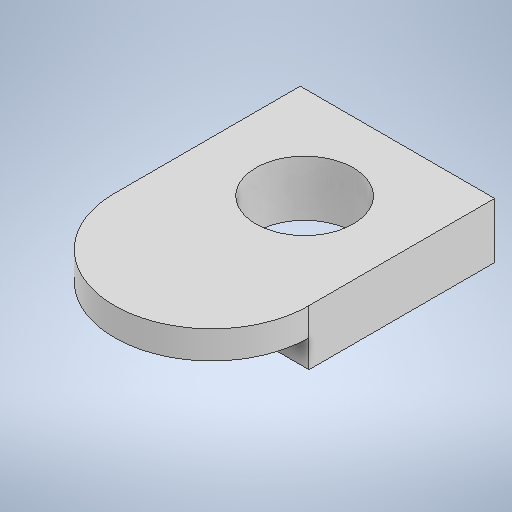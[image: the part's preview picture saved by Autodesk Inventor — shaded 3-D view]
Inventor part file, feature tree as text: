
AUTODESK INVENTOR PART (.ipt)
format: ipt  version: 2025 (Build 290162000, 162)  size: 218,112 bytes
history: native  units: in
note: dims shown in document units (in); Inventor stores cm internally (conversion verified against a paired STEP export)
features: extrude x2, sketch x2, projected_geometry x1
ambient origin geometry x8: Origin, YZ Plane, XZ Plane, XY Plane, X Axis, Y Axis, Z Axis, Center Point
bodies: Solid1 (feature_tree)
feature tree (5):
  extrude  "Extrusion1"  Depth=0.2631in
  extrude  "Extrusion2"  Depth=0.1378in
  sketch  "Sketch1"  dims[d0=0.2756in d1=0.2631in]
  sketch  "Sketch2"  dims[d2=0.1316in d3=0.1378in d4=0.0394in d5=0.0in d6=0.0394in d7=0.0in]
  projected_geometry  "Projected Loop1"
